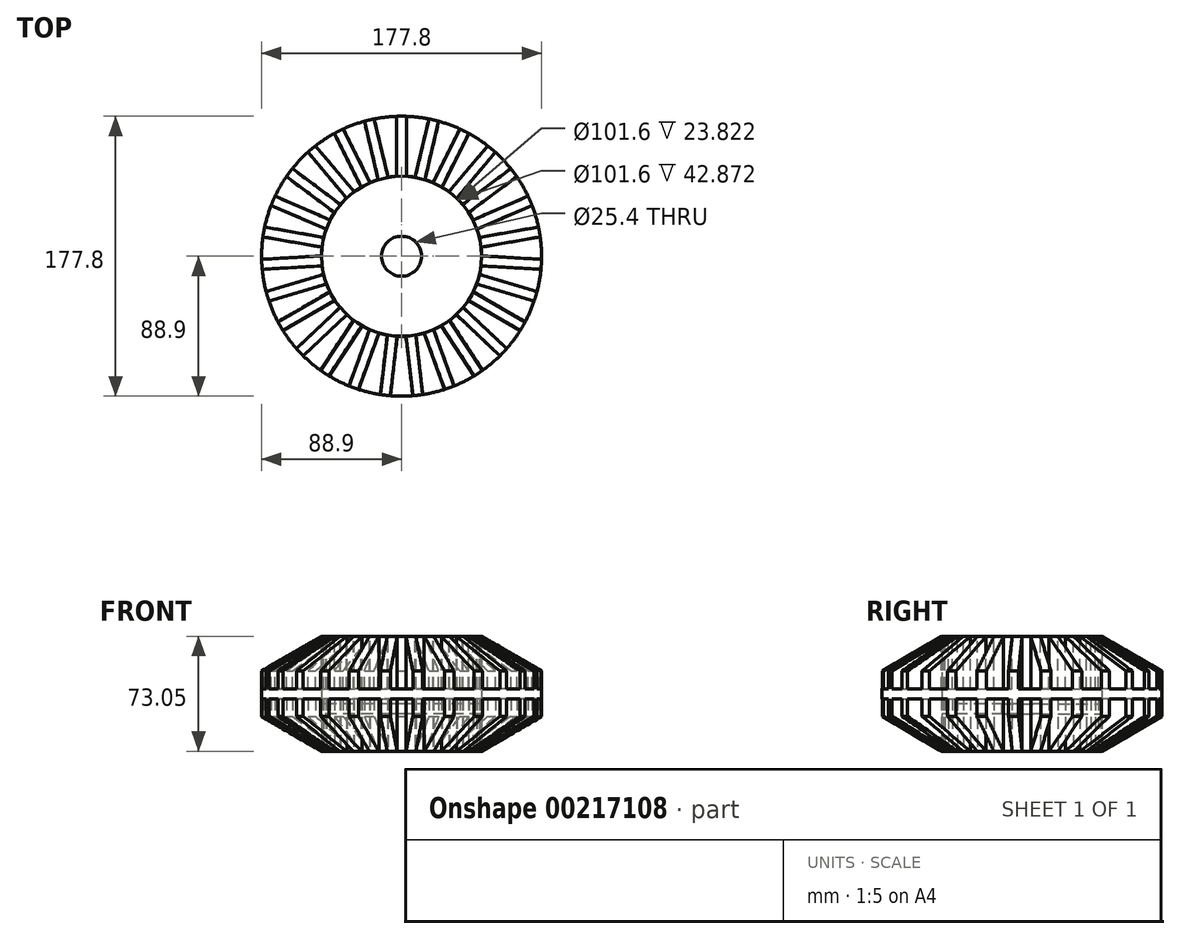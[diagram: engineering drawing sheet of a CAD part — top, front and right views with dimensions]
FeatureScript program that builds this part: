
annotation { "Feature Type Name" : "Feature", "Feature Type Description" : "" }
export const myFeature = defineFeature(function(context is Context, id is Id, definition is map)
    precondition{}
    {
        {
            var Q0;
            Q0=qCreatedBy(makeId("Top.planeOp"),FACE);
            var sketch = newSketch(context, id + "F0", { "sketchPlane" : qUnion([Q0])});
            skCircle(sketch, "E0", {"center": v(0, 0) * mm, "radius": 88.9 * mm});
            skCircle(sketch, "E1", {"center": v(0, 0) * mm, "radius": 50.8 * mm});
            skLineSegment(sketch, "E2.bottom", {"start": v(104.67, -12.7) * mm, "end": v(98.32, -12.7) * mm});
            skLineSegment(sketch, "E2.top", {"start": v(104.67, 12.7) * mm, "end": v(98.32, 12.7) * mm});
            skLineSegment(sketch, "E2.left", {"start": v(104.67, -12.7) * mm, "end": v(104.67, 12.7) * mm});
            skLineSegment(sketch, "E2.right", {"start": v(98.32, -12.7) * mm, "end": v(98.32, 12.7) * mm});
            skPoint(sketch, "E2.middle", {"position": v(101.5, 0) * mm});
            skSolve(sketch);
        }
        {
            var Q0;
            Q0=makeQuery(id+"F0.imprint","IMPRINT",FACE,{"disambiguationData":[TD([[makeQuery(id+"F0.imprint","IMPRINT",EDGE,{"derivedFrom":sQuery(id+"F0.wireOp",EDGE,"E0")}),1.0]])]});
            extrude(context, id + "F1", {"entities" : qUnion([Q0]), "depth" : 50.8 * mm});
        }
        {
            var Q0;
            Q0=makeQuery(id+"F0.imprint","IMPRINT",FACE,{"disambiguationData":[TD([[makeQuery(id+"F0.imprint","IMPRINT",EDGE,{"derivedFrom":sQuery(id+"F0.wireOp",EDGE,"E1")}),1.0]])]});
            extrude(context, id + "F2", {"entities" : qUnion([Q0]), "operationType" : NewBodyOperationType.ADD, "depth" : 6.35 * mm});
        }
        {
            var Q0;
            Q0=makeQuery(id+"F1.opExtrude","CAP_FACE",FACE,{"disambiguationData":[OSD([sQuery(id+"F0.wireOp",EDGE,"E0"),sQuery(id+"F0.wireOp",EDGE,"E1")])],"isStart":false});
            var sketch = newSketch(context, id + "F3", { "sketchPlane" : qUnion([Q0])});
            skLineSegment(sketch, "E3.0", {"start": v(-3.18, 88.9) * mm, "end": v(-3.17, 50.8) * mm});
            skLineSegment(sketch, "E4.0", {"start": v(3.18, 88.9) * mm, "end": v(3.18, 50.8) * mm});
            skPoint(sketch, "E5.start.orphan", {"position": v(0, 88.9) * mm});
            skLineSegment(sketch, "E6.1.0", {"start": v(-17.41, 87.24) * mm, "end": v(-8.63, 50.16) * mm});
            skLineSegment(sketch, "E6.1.1", {"start": v(-23.6, 85.77) * mm, "end": v(-14.8, 48.7) * mm});
            skLineSegment(sketch, "E6.2.0", {"start": v(-37.06, 80.87) * mm, "end": v(-19.96, 46.82) * mm});
            skLineSegment(sketch, "E6.2.1", {"start": v(-42.74, 78.02) * mm, "end": v(-25.64, 43.97) * mm});
            skLineSegment(sketch, "E6.3.0", {"start": v(-54.71, 70.14) * mm, "end": v(-30.22, 40.96) * mm});
            skLineSegment(sketch, "E6.3.1", {"start": v(-59.58, 66.06) * mm, "end": v(-35.09, 36.87) * mm});
            skLineSegment(sketch, "E6.4.0", {"start": v(-69.41, 55.63) * mm, "end": v(-38.85, 32.88) * mm});
            skLineSegment(sketch, "E6.4.1", {"start": v(-73.2, 50.54) * mm, "end": v(-42.64, 27.79) * mm});
            skLineSegment(sketch, "E6.5.0", {"start": v(-80.37, 38.13) * mm, "end": v(-45.39, 23.04) * mm});
            skLineSegment(sketch, "E6.5.1", {"start": v(-82.89, 32.3) * mm, "end": v(-47.9, 17.2) * mm});
            skLineSegment(sketch, "E6.6.0", {"start": v(-87, 18.56) * mm, "end": v(-49.48, 11.95) * mm});
            skLineSegment(sketch, "E6.6.1", {"start": v(-88.1, 12.31) * mm, "end": v(-50.58, 5.7) * mm});
            skLineSegment(sketch, "E6.7.0", {"start": v(-88.93, -2) * mm, "end": v(-50.9, 0.22) * mm});
            skLineSegment(sketch, "E6.7.1", {"start": v(-88.56, -8.34) * mm, "end": v(-50.53, -6.12) * mm});
            skLineSegment(sketch, "E6.8.0", {"start": v(-86.08, -22.46) * mm, "end": v(-49.58, -11.53) * mm});
            skLineSegment(sketch, "E6.8.1", {"start": v(-84.25, -28.54) * mm, "end": v(-47.76, -17.61) * mm});
            skLineSegment(sketch, "E6.9.0", {"start": v(-78.58, -41.7) * mm, "end": v(-45.58, -22.65) * mm});
            skLineSegment(sketch, "E6.9.1", {"start": v(-75.4, -47.2) * mm, "end": v(-42.4, -28.15) * mm});
            skLineSegment(sketch, "E6.10.0", {"start": v(-66.84, -58.7) * mm, "end": v(-39.13, -32.55) * mm});
            skLineSegment(sketch, "E6.10.1", {"start": v(-62.48, -63.32) * mm, "end": v(-34.77, -37.17) * mm});
            skLineSegment(sketch, "E6.11.0", {"start": v(-51.5, -72.53) * mm, "end": v(-30.57, -40.7) * mm});
            skLineSegment(sketch, "E6.11.1", {"start": v(-46.2, -76.02) * mm, "end": v(-25.26, -44.19) * mm});
            skLineSegment(sketch, "E6.12.0", {"start": v(-33.39, -82.45) * mm, "end": v(-20.36, -46.65) * mm});
            skLineSegment(sketch, "E6.12.1", {"start": v(-27.42, -84.62) * mm, "end": v(-14.4, -48.82) * mm});
            skLineSegment(sketch, "E6.13.0", {"start": v(-13.47, -87.93) * mm, "end": v(-9.05, -50.09) * mm});
            skLineSegment(sketch, "E6.13.1", {"start": v(-7.17, -88.67) * mm, "end": v(-2.74, -50.83) * mm});
            skLineSegment(sketch, "E6.14.0", {"start": v(7.17, -88.67) * mm, "end": v(2.74, -50.83) * mm});
            skLineSegment(sketch, "E6.14.1", {"start": v(13.47, -87.93) * mm, "end": v(9.05, -50.09) * mm});
            skLineSegment(sketch, "E6.15.0", {"start": v(27.42, -84.62) * mm, "end": v(14.4, -48.82) * mm});
            skLineSegment(sketch, "E6.15.1", {"start": v(33.39, -82.45) * mm, "end": v(20.36, -46.65) * mm});
            skLineSegment(sketch, "E6.16.0", {"start": v(46.2, -76.02) * mm, "end": v(25.26, -44.19) * mm});
            skLineSegment(sketch, "E6.16.1", {"start": v(51.5, -72.53) * mm, "end": v(30.57, -40.7) * mm});
            skLineSegment(sketch, "E6.17.0", {"start": v(62.48, -63.32) * mm, "end": v(34.77, -37.17) * mm});
            skLineSegment(sketch, "E6.17.1", {"start": v(66.84, -58.7) * mm, "end": v(39.13, -32.55) * mm});
            skLineSegment(sketch, "E6.18.0", {"start": v(75.4, -47.2) * mm, "end": v(42.4, -28.15) * mm});
            skLineSegment(sketch, "E6.18.1", {"start": v(78.58, -41.7) * mm, "end": v(45.58, -22.65) * mm});
            skLineSegment(sketch, "E6.19.0", {"start": v(84.25, -28.54) * mm, "end": v(47.76, -17.61) * mm});
            skLineSegment(sketch, "E6.19.1", {"start": v(86.08, -22.46) * mm, "end": v(49.58, -11.53) * mm});
            skLineSegment(sketch, "E6.20.0", {"start": v(88.56, -8.34) * mm, "end": v(50.53, -6.12) * mm});
            skLineSegment(sketch, "E6.20.1", {"start": v(88.93, -2) * mm, "end": v(50.9, 0.22) * mm});
            skLineSegment(sketch, "E6.21.0", {"start": v(88.1, 12.31) * mm, "end": v(50.58, 5.7) * mm});
            skLineSegment(sketch, "E6.21.1", {"start": v(87, 18.56) * mm, "end": v(49.48, 11.95) * mm});
            skLineSegment(sketch, "E6.22.0", {"start": v(82.89, 32.3) * mm, "end": v(47.9, 17.2) * mm});
            skLineSegment(sketch, "E6.22.1", {"start": v(80.37, 38.13) * mm, "end": v(45.39, 23.04) * mm});
            skLineSegment(sketch, "E6.23.0", {"start": v(73.2, 50.54) * mm, "end": v(42.64, 27.79) * mm});
            skLineSegment(sketch, "E6.23.1", {"start": v(69.41, 55.63) * mm, "end": v(38.85, 32.88) * mm});
            skLineSegment(sketch, "E6.24.0", {"start": v(59.58, 66.06) * mm, "end": v(35.09, 36.87) * mm});
            skLineSegment(sketch, "E6.24.1", {"start": v(54.71, 70.14) * mm, "end": v(30.22, 40.96) * mm});
            skLineSegment(sketch, "E6.25.0", {"start": v(42.74, 78.02) * mm, "end": v(25.64, 43.97) * mm});
            skLineSegment(sketch, "E6.25.1", {"start": v(37.06, 80.87) * mm, "end": v(19.96, 46.82) * mm});
            skLineSegment(sketch, "E6.26.0", {"start": v(23.6, 85.77) * mm, "end": v(14.8, 48.7) * mm});
            skLineSegment(sketch, "E6.26.1", {"start": v(17.41, 87.24) * mm, "end": v(8.63, 50.16) * mm});
            skPoint(sketch, "E6.center", {"position": v(0, 0) * mm});
            skCircle(sketch, "E7", {"center": v(0, 0) * mm, "radius": 50.9 * mm});
            skCircle(sketch, "E8", {"center": v(0, 0) * mm, "radius": 88.96 * mm});
            skSolve(sketch);
        }
        {
            var Q0;
            {var subQ0=sQuery(id+"F3.wireOp",EDGE,"E7");var subQ1=sQuery(id+"F3.wireOp",EDGE,"E6.24.1");var subQ2=makeQuery(id+"F3.imprint","INTERSECT",VERTEX,{"derivedFrom":[subQ1,subQ0]});Q0=makeQuery(id+"F3.imprint","IMPRINT",FACE,{"disambiguationData":[TD([[makeQuery(id+"F3.imprint","IMPRINT",EDGE,{"disambiguationData":[TD([[subQ2,1.0]])],"derivedFrom":subQ1}),-1.0]])]});}
            var Q1;
            {var subQ0=sQuery(id+"F3.wireOp",EDGE,"E7");var subQ1=sQuery(id+"F3.wireOp",EDGE,"E6.25.1");var subQ2=makeQuery(id+"F3.imprint","INTERSECT",VERTEX,{"derivedFrom":[subQ1,subQ0]});Q1=makeQuery(id+"F3.imprint","IMPRINT",FACE,{"disambiguationData":[TD([[makeQuery(id+"F3.imprint","IMPRINT",EDGE,{"disambiguationData":[TD([[subQ2,1.0]])],"derivedFrom":subQ1}),-1.0]])]});}
            var Q2;
            {var subQ0=sQuery(id+"F3.wireOp",EDGE,"E7");var subQ1=sQuery(id+"F3.wireOp",EDGE,"E4.0");var subQ2=makeQuery(id+"F3.imprint","INTERSECT",VERTEX,{"derivedFrom":[subQ1,subQ0]});Q2=makeQuery(id+"F3.imprint","IMPRINT",FACE,{"disambiguationData":[TD([[makeQuery(id+"F3.imprint","IMPRINT",EDGE,{"disambiguationData":[TD([[subQ2,1.0]])],"derivedFrom":subQ1}),1.0]])]});}
            var Q3;
            {var subQ0=sQuery(id+"F3.wireOp",EDGE,"E7");var subQ1=sQuery(id+"F3.wireOp",EDGE,"E3.0");var subQ2=makeQuery(id+"F3.imprint","INTERSECT",VERTEX,{"derivedFrom":[subQ1,subQ0]});Q3=makeQuery(id+"F3.imprint","IMPRINT",FACE,{"disambiguationData":[TD([[makeQuery(id+"F3.imprint","IMPRINT",EDGE,{"disambiguationData":[TD([[subQ2,1.0]])],"derivedFrom":subQ1}),-1.0]])]});}
            var Q4;
            {var subQ0=sQuery(id+"F3.wireOp",EDGE,"E7");var subQ1=sQuery(id+"F3.wireOp",EDGE,"E6.1.1");var subQ2=makeQuery(id+"F3.imprint","INTERSECT",VERTEX,{"derivedFrom":[subQ1,subQ0]});Q4=makeQuery(id+"F3.imprint","IMPRINT",FACE,{"disambiguationData":[TD([[makeQuery(id+"F3.imprint","IMPRINT",EDGE,{"disambiguationData":[TD([[subQ2,1.0]])],"derivedFrom":subQ1}),-1.0]])]});}
            var Q5;
            {var subQ0=sQuery(id+"F3.wireOp",EDGE,"E7");var subQ1=sQuery(id+"F3.wireOp",EDGE,"E6.2.1");var subQ2=makeQuery(id+"F3.imprint","INTERSECT",VERTEX,{"derivedFrom":[subQ1,subQ0]});Q5=makeQuery(id+"F3.imprint","IMPRINT",FACE,{"disambiguationData":[TD([[makeQuery(id+"F3.imprint","IMPRINT",EDGE,{"disambiguationData":[TD([[subQ2,1.0]])],"derivedFrom":subQ1}),-1.0]])]});}
            var Q6;
            {var subQ0=sQuery(id+"F3.wireOp",EDGE,"E7");var subQ1=sQuery(id+"F3.wireOp",EDGE,"E6.3.1");var subQ2=makeQuery(id+"F3.imprint","INTERSECT",VERTEX,{"derivedFrom":[subQ1,subQ0]});Q6=makeQuery(id+"F3.imprint","IMPRINT",FACE,{"disambiguationData":[TD([[makeQuery(id+"F3.imprint","IMPRINT",EDGE,{"disambiguationData":[TD([[subQ2,1.0]])],"derivedFrom":subQ1}),-1.0]])]});}
            var Q7;
            {var subQ0=sQuery(id+"F3.wireOp",EDGE,"E7");var subQ1=sQuery(id+"F3.wireOp",EDGE,"E6.4.1");var subQ2=makeQuery(id+"F3.imprint","INTERSECT",VERTEX,{"derivedFrom":[subQ1,subQ0]});Q7=makeQuery(id+"F3.imprint","IMPRINT",FACE,{"disambiguationData":[TD([[makeQuery(id+"F3.imprint","IMPRINT",EDGE,{"disambiguationData":[TD([[subQ2,1.0]])],"derivedFrom":subQ1}),-1.0]])]});}
            var Q8;
            {var subQ0=sQuery(id+"F3.wireOp",EDGE,"E7");var subQ1=sQuery(id+"F3.wireOp",EDGE,"E6.5.1");var subQ2=makeQuery(id+"F3.imprint","INTERSECT",VERTEX,{"derivedFrom":[subQ1,subQ0]});Q8=makeQuery(id+"F3.imprint","IMPRINT",FACE,{"disambiguationData":[TD([[makeQuery(id+"F3.imprint","IMPRINT",EDGE,{"disambiguationData":[TD([[subQ2,1.0]])],"derivedFrom":subQ1}),-1.0]])]});}
            var Q9;
            {var subQ0=sQuery(id+"F3.wireOp",EDGE,"E7");var subQ1=sQuery(id+"F3.wireOp",EDGE,"E6.6.1");var subQ2=makeQuery(id+"F3.imprint","INTERSECT",VERTEX,{"derivedFrom":[subQ1,subQ0]});Q9=makeQuery(id+"F3.imprint","IMPRINT",FACE,{"disambiguationData":[TD([[makeQuery(id+"F3.imprint","IMPRINT",EDGE,{"disambiguationData":[TD([[subQ2,1.0]])],"derivedFrom":subQ1}),-1.0]])]});}
            var Q10;
            {var subQ0=sQuery(id+"F3.wireOp",EDGE,"E7");var subQ1=sQuery(id+"F3.wireOp",EDGE,"E6.7.1");var subQ2=makeQuery(id+"F3.imprint","INTERSECT",VERTEX,{"derivedFrom":[subQ1,subQ0]});Q10=makeQuery(id+"F3.imprint","IMPRINT",FACE,{"disambiguationData":[TD([[makeQuery(id+"F3.imprint","IMPRINT",EDGE,{"disambiguationData":[TD([[subQ2,1.0]])],"derivedFrom":subQ1}),-1.0]])]});}
            var Q11;
            {var subQ0=sQuery(id+"F3.wireOp",EDGE,"E7");var subQ1=sQuery(id+"F3.wireOp",EDGE,"E6.8.1");var subQ2=makeQuery(id+"F3.imprint","INTERSECT",VERTEX,{"derivedFrom":[subQ1,subQ0]});Q11=makeQuery(id+"F3.imprint","IMPRINT",FACE,{"disambiguationData":[TD([[makeQuery(id+"F3.imprint","IMPRINT",EDGE,{"disambiguationData":[TD([[subQ2,1.0]])],"derivedFrom":subQ1}),-1.0]])]});}
            var Q12;
            {var subQ0=sQuery(id+"F3.wireOp",EDGE,"E7");var subQ1=sQuery(id+"F3.wireOp",EDGE,"E6.9.1");var subQ2=makeQuery(id+"F3.imprint","INTERSECT",VERTEX,{"derivedFrom":[subQ1,subQ0]});Q12=makeQuery(id+"F3.imprint","IMPRINT",FACE,{"disambiguationData":[TD([[makeQuery(id+"F3.imprint","IMPRINT",EDGE,{"disambiguationData":[TD([[subQ2,1.0]])],"derivedFrom":subQ1}),-1.0]])]});}
            var Q13;
            {var subQ0=sQuery(id+"F3.wireOp",EDGE,"E7");var subQ1=sQuery(id+"F3.wireOp",EDGE,"E6.10.1");var subQ2=makeQuery(id+"F3.imprint","INTERSECT",VERTEX,{"derivedFrom":[subQ1,subQ0]});Q13=makeQuery(id+"F3.imprint","IMPRINT",FACE,{"disambiguationData":[TD([[makeQuery(id+"F3.imprint","IMPRINT",EDGE,{"disambiguationData":[TD([[subQ2,1.0]])],"derivedFrom":subQ1}),-1.0]])]});}
            var Q14;
            {var subQ0=sQuery(id+"F3.wireOp",EDGE,"E7");var subQ1=sQuery(id+"F3.wireOp",EDGE,"E6.11.1");var subQ2=makeQuery(id+"F3.imprint","INTERSECT",VERTEX,{"derivedFrom":[subQ1,subQ0]});Q14=makeQuery(id+"F3.imprint","IMPRINT",FACE,{"disambiguationData":[TD([[makeQuery(id+"F3.imprint","IMPRINT",EDGE,{"disambiguationData":[TD([[subQ2,1.0]])],"derivedFrom":subQ1}),-1.0]])]});}
            var Q15;
            {var subQ0=sQuery(id+"F3.wireOp",EDGE,"E7");var subQ1=sQuery(id+"F3.wireOp",EDGE,"E6.12.1");var subQ2=makeQuery(id+"F3.imprint","INTERSECT",VERTEX,{"derivedFrom":[subQ1,subQ0]});Q15=makeQuery(id+"F3.imprint","IMPRINT",FACE,{"disambiguationData":[TD([[makeQuery(id+"F3.imprint","IMPRINT",EDGE,{"disambiguationData":[TD([[subQ2,1.0]])],"derivedFrom":subQ1}),-1.0]])]});}
            var Q16;
            {var subQ0=sQuery(id+"F3.wireOp",EDGE,"E7");var subQ1=sQuery(id+"F3.wireOp",EDGE,"E6.13.1");var subQ2=makeQuery(id+"F3.imprint","INTERSECT",VERTEX,{"derivedFrom":[subQ1,subQ0]});Q16=makeQuery(id+"F3.imprint","IMPRINT",FACE,{"disambiguationData":[TD([[makeQuery(id+"F3.imprint","IMPRINT",EDGE,{"disambiguationData":[TD([[subQ2,1.0]])],"derivedFrom":subQ1}),-1.0]])]});}
            var Q17;
            {var subQ0=sQuery(id+"F3.wireOp",EDGE,"E7");var subQ1=sQuery(id+"F3.wireOp",EDGE,"E6.14.1");var subQ2=makeQuery(id+"F3.imprint","INTERSECT",VERTEX,{"derivedFrom":[subQ1,subQ0]});Q17=makeQuery(id+"F3.imprint","IMPRINT",FACE,{"disambiguationData":[TD([[makeQuery(id+"F3.imprint","IMPRINT",EDGE,{"disambiguationData":[TD([[subQ2,1.0]])],"derivedFrom":subQ1}),-1.0]])]});}
            var Q18;
            {var subQ0=sQuery(id+"F3.wireOp",EDGE,"E7");var subQ1=sQuery(id+"F3.wireOp",EDGE,"E6.15.1");var subQ2=makeQuery(id+"F3.imprint","INTERSECT",VERTEX,{"derivedFrom":[subQ1,subQ0]});Q18=makeQuery(id+"F3.imprint","IMPRINT",FACE,{"disambiguationData":[TD([[makeQuery(id+"F3.imprint","IMPRINT",EDGE,{"disambiguationData":[TD([[subQ2,1.0]])],"derivedFrom":subQ1}),-1.0]])]});}
            var Q19;
            {var subQ0=sQuery(id+"F3.wireOp",EDGE,"E7");var subQ1=sQuery(id+"F3.wireOp",EDGE,"E6.16.1");var subQ2=makeQuery(id+"F3.imprint","INTERSECT",VERTEX,{"derivedFrom":[subQ1,subQ0]});Q19=makeQuery(id+"F3.imprint","IMPRINT",FACE,{"disambiguationData":[TD([[makeQuery(id+"F3.imprint","IMPRINT",EDGE,{"disambiguationData":[TD([[subQ2,1.0]])],"derivedFrom":subQ1}),-1.0]])]});}
            var Q20;
            {var subQ0=sQuery(id+"F3.wireOp",EDGE,"E7");var subQ1=sQuery(id+"F3.wireOp",EDGE,"E6.17.1");var subQ2=makeQuery(id+"F3.imprint","INTERSECT",VERTEX,{"derivedFrom":[subQ1,subQ0]});Q20=makeQuery(id+"F3.imprint","IMPRINT",FACE,{"disambiguationData":[TD([[makeQuery(id+"F3.imprint","IMPRINT",EDGE,{"disambiguationData":[TD([[subQ2,1.0]])],"derivedFrom":subQ1}),-1.0]])]});}
            var Q21;
            {var subQ0=sQuery(id+"F3.wireOp",EDGE,"E7");var subQ1=sQuery(id+"F3.wireOp",EDGE,"E6.18.1");var subQ2=makeQuery(id+"F3.imprint","INTERSECT",VERTEX,{"derivedFrom":[subQ1,subQ0]});Q21=makeQuery(id+"F3.imprint","IMPRINT",FACE,{"disambiguationData":[TD([[makeQuery(id+"F3.imprint","IMPRINT",EDGE,{"disambiguationData":[TD([[subQ2,1.0]])],"derivedFrom":subQ1}),-1.0]])]});}
            var Q22;
            {var subQ0=sQuery(id+"F3.wireOp",EDGE,"E7");var subQ1=sQuery(id+"F3.wireOp",EDGE,"E6.19.1");var subQ2=makeQuery(id+"F3.imprint","INTERSECT",VERTEX,{"derivedFrom":[subQ1,subQ0]});Q22=makeQuery(id+"F3.imprint","IMPRINT",FACE,{"disambiguationData":[TD([[makeQuery(id+"F3.imprint","IMPRINT",EDGE,{"disambiguationData":[TD([[subQ2,1.0]])],"derivedFrom":subQ1}),-1.0]])]});}
            var Q23;
            {var subQ0=sQuery(id+"F3.wireOp",EDGE,"E7");var subQ1=sQuery(id+"F3.wireOp",EDGE,"E6.20.1");var subQ2=makeQuery(id+"F3.imprint","INTERSECT",VERTEX,{"derivedFrom":[subQ1,subQ0]});Q23=makeQuery(id+"F3.imprint","IMPRINT",FACE,{"disambiguationData":[TD([[makeQuery(id+"F3.imprint","IMPRINT",EDGE,{"disambiguationData":[TD([[subQ2,1.0]])],"derivedFrom":subQ1}),-1.0]])]});}
            var Q24;
            {var subQ0=sQuery(id+"F3.wireOp",EDGE,"E7");var subQ1=sQuery(id+"F3.wireOp",EDGE,"E6.21.1");var subQ2=makeQuery(id+"F3.imprint","INTERSECT",VERTEX,{"derivedFrom":[subQ1,subQ0]});Q24=makeQuery(id+"F3.imprint","IMPRINT",FACE,{"disambiguationData":[TD([[makeQuery(id+"F3.imprint","IMPRINT",EDGE,{"disambiguationData":[TD([[subQ2,1.0]])],"derivedFrom":subQ1}),-1.0]])]});}
            var Q25;
            {var subQ0=sQuery(id+"F3.wireOp",EDGE,"E7");var subQ1=sQuery(id+"F3.wireOp",EDGE,"E6.22.1");var subQ2=makeQuery(id+"F3.imprint","INTERSECT",VERTEX,{"derivedFrom":[subQ1,subQ0]});Q25=makeQuery(id+"F3.imprint","IMPRINT",FACE,{"disambiguationData":[TD([[makeQuery(id+"F3.imprint","IMPRINT",EDGE,{"disambiguationData":[TD([[subQ2,1.0]])],"derivedFrom":subQ1}),-1.0]])]});}
            var Q26;
            {var subQ0=sQuery(id+"F3.wireOp",EDGE,"E7");var subQ1=sQuery(id+"F3.wireOp",EDGE,"E6.23.1");var subQ2=makeQuery(id+"F3.imprint","INTERSECT",VERTEX,{"derivedFrom":[subQ1,subQ0]});Q26=makeQuery(id+"F3.imprint","IMPRINT",FACE,{"disambiguationData":[TD([[makeQuery(id+"F3.imprint","IMPRINT",EDGE,{"disambiguationData":[TD([[subQ2,1.0]])],"derivedFrom":subQ1}),-1.0]])]});}
            var Q27;
            Q27=makeQuery(id+"F3.imprint","IMPRINT",FACE,{"disambiguationData":[TD([[makeQuery(id+"F3.imprint","IMPRINT",EDGE,{"derivedFrom":makeQuery(id+"F1.opExtrude","CAP_EDGE",EDGE,{"disambiguationData":[OSD([sQuery(id+"F0.wireOp",EDGE,"E1")])],"isStart":false})}),1.0]])]});
            extrude(context, id + "F4", {"entities" : qUnion([Q0, Q1, Q2, Q3, Q4, Q5, Q6, Q7, Q8, Q9, Q10, Q11, Q12, Q13, Q14, Q15, Q16, Q17, Q18, Q19, Q20, Q21, Q22, Q23, Q24, Q25, Q26, Q27]), "operationType" : NewBodyOperationType.REMOVE, "oppositeDirection" : true, "depth" : 38.1 * mm});
        }
        {
            var Q0;
            Q0=qCreatedBy(makeId("Front.planeOp"),FACE);
            var sketch = newSketch(context, id + "F5", { "sketchPlane" : qUnion([Q0])});
            skLineSegment(sketch, "E9", {"start": v(89.9, 0) * mm, "end": v(89.9, 23.48) * mm});
            skLineSegment(sketch, "E10", {"start": v(89.9, 23.48) * mm, "end": v(41.8, 51.25) * mm});
            skLineSegment(sketch, "E11", {"start": v(41.8, 51.25) * mm, "end": v(107.98, 74.03) * mm});
            skLineSegment(sketch, "E12", {"start": v(107.98, 74.03) * mm, "end": v(154.62, -12.88) * mm});
            skLineSegment(sketch, "E13", {"start": v(154.62, -12.88) * mm, "end": v(91.48, -12.88) * mm});
            skLineSegment(sketch, "E14", {"start": v(91.48, -12.88) * mm, "end": v(89.9, 0) * mm});
            skSolve(sketch);
        }
        {
            var Q0;
            Q0 = qSketchRegion(id + "F5", true);
            var Q1;
            Q1=makeQuery(id+"F1.opExtrude","CAP_EDGE",EDGE,{"disambiguationData":[OSD([sQuery(id+"F0.wireOp",EDGE,"E0")])],"isStart":true});
            revolve(context, id + "F6", {"operationType" : NewBodyOperationType.REMOVE, "entities" : qUnion([Q0]), "axis" : qUnion([Q1]), "revolveType" : RevolveType.FULL, "oppositeDirection" : true});
        }
        {
            var Q0;
            Q0=makeQuery(id+"F2.opExtrude","CAP_FACE",FACE,{"disambiguationData":[OSD([sQuery(id+"F0.wireOp",EDGE,"E1")])],"isStart":false});
            var sketch = newSketch(context, id + "F7", { "sketchPlane" : qUnion([Q0])});
            skCircle(sketch, "E15", {"center": v(0, 0) * mm, "radius": 12.7 * mm});
            skSolve(sketch);
        }
        {
            var Q0;
            Q0=makeQuery(id+"F7.imprint","IMPRINT",FACE,{"disambiguationData":[TD([[makeQuery(id+"F7.imprint","IMPRINT",EDGE,{"derivedFrom":sQuery(id+"F7.wireOp",EDGE,"E15")}),1.0]])]});
            extrude(context, id + "F8", {"entities" : qUnion([Q0]), "operationType" : NewBodyOperationType.REMOVE, "oppositeDirection" : true, "depth" : 25.4 * mm});
        }
        {
            var Q0;
            {var subQ0=sQuery(id+"F0.wireOp",EDGE,"E1");Q0=makeQuery(id+"F2.boolean.opBoolean","MERGE",FACE,{"derivedFrom":[makeQuery(id+"F1.opExtrude","CAP_FACE",FACE,{"disambiguationData":[OSD([sQuery(id+"F0.wireOp",EDGE,"E0"),subQ0])],"isStart":true}),makeQuery(id+"F2.opExtrude","CAP_FACE",FACE,{"disambiguationData":[OSD([subQ0])],"isStart":true})]});}
            extrude(context, id + "F9", {"entities" : qUnion([Q0]), "operationType" : NewBodyOperationType.REMOVE, "oppositeDirection" : true, "depth" : 9.52 * mm});
        }
        {
            var Q0;
            Q0=makeQuery(id+"F1.opExtrude","SWEPT_BODY",BODY,{"disambiguationData":[OSD([sQuery(id+"F0.wireOp",EDGE,"E0"),sQuery(id+"F0.wireOp",EDGE,"E1")])]});
            var Q1;
            Q1=makeQuery(id+"F9.boolean.opBoolean","COPY",FACE,{"derivedFrom":makeQuery(id+"F9.opExtrude","CAP_FACE",FACE,{"disambiguationData":[OSD([sQuery(id+"F0.wireOp",EDGE,"E0"),sQuery(id+"F0.wireOp",EDGE,"E1")])],"isStart":false})});
            mirror(context, id + "F10", {"operationType" : NewBodyOperationType.ADD, "entities" : qUnion([Q0]), "mirrorPlane" : qUnion([Q1])});
        }
        {
            var Q0;
            Q0=qCreatedBy(makeId("Top.planeOp"),FACE);
            var sketch = newSketch(context, id + "F11", { "sketchPlane" : qUnion([Q0])});
            skCircle(sketch, "E16", {"center": v(0, 0) * mm, "radius": 50.8 * mm});
            skSolve(sketch);
        }
        {
            var Q0;
            Q0 = qSketchRegion(id + "F11", true);
            extrude(context, id + "F12", {"entities" : qUnion([Q0]), "operationType" : NewBodyOperationType.ADD, "depth" : 6.35 * mm, "symmetric" : true});
        }
        {
            var Q0;
            Q0=makeQuery(id+"F12.opExtrude","CAP_FACE",FACE,{"disambiguationData":[OSD([sQuery(id+"F11.wireOp",EDGE,"E16")])],"isStart":false});
            var sketch = newSketch(context, id + "F13", { "sketchPlane" : qUnion([Q0])});
            skCircle(sketch, "E17", {"center": v(0, 0) * mm, "radius": 12.7 * mm});
            skSolve(sketch);
        }
        {
            var Q0;
            Q0=makeQuery(id+"F13.imprint","IMPRINT",FACE,{"disambiguationData":[TD([[makeQuery(id+"F13.imprint","IMPRINT",EDGE,{"derivedFrom":sQuery(id+"F13.wireOp",EDGE,"E17")}),1.0]])]});
            extrude(context, id + "F14", {"entities" : qUnion([Q0]), "operationType" : NewBodyOperationType.REMOVE, "oppositeDirection" : true, "depth" : 25.4 * mm});
        }
    });
